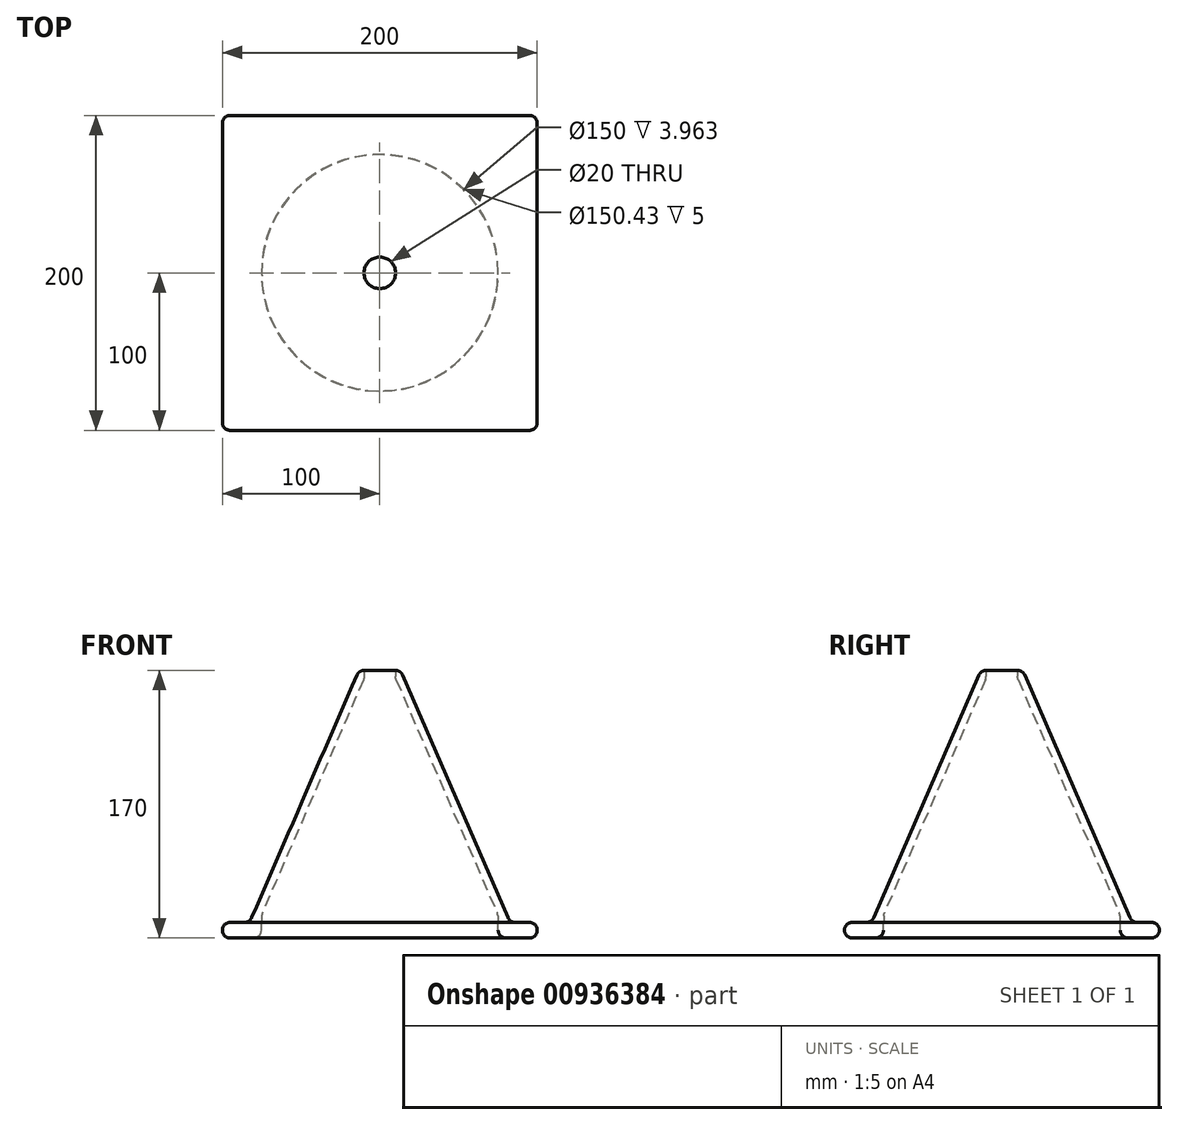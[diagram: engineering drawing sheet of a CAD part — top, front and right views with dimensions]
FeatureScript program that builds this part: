
annotation { "Feature Type Name" : "Feature", "Feature Type Description" : "" }
export const myFeature = defineFeature(function(context is Context, id is Id, definition is map)
    precondition{}
    {
        {
            var Q0;
            Q0=qCreatedBy(makeId("Front.planeOp"),FACE);
            var sketch = newSketch(context, id + "F0", { "sketchPlane" : qUnion([Q0])});
            skPoint(sketch, "E0.middle", {"position": v(0, 0) * mm});
            skLineSegment(sketch, "E1", {"start": v(-10, 75) * mm, "end": v(-75, -75) * mm});
            skLineSegment(sketch, "E2.0", {"start": v(-82.62, -80) * mm, "end": v(-75, -80) * mm});
            skLineSegment(sketch, "E2.1", {"start": v(-13.28, 80) * mm, "end": v(-82.62, -80) * mm});
            skLineSegment(sketch, "E3", {"start": v(-10, 75) * mm, "end": v(-10, 80) * mm});
            skLineSegment(sketch, "E4", {"start": v(-13.28, 80) * mm, "end": v(-10, 80) * mm});
            skLineSegment(sketch, "E5", {"start": v(-75, -75) * mm, "end": v(-75, -80) * mm});
            skLineSegment(sketch, "E6", {"start": v(0, -85.18) * mm, "end": v(0, 91.02) * mm});
            skSolve(sketch);
        }
        {
            var Q0;
            Q0=makeQuery(id+"F0.imprint","IMPRINT",FACE,{"disambiguationData":[TD([[makeQuery(id+"F0.imprint","IMPRINT",EDGE,{"derivedFrom":sQuery(id+"F0.wireOp",EDGE,"E1")}),-1.0]])]});
            var Q1;
            Q1=sQuery(id+"F0.wireOp",EDGE,"E6");
            revolve(context, id + "F1", {"surfaceOperationType" : NewSurfaceOperationType.NEW, "entities" : qUnion([Q0]), "axis" : qUnion([Q1]), "revolveType" : RevolveType.FULL});
        }
        {
            var Q0;
            Q0=makeQuery(id+"F1.opRevolve","SWEPT_FACE",FACE,{"disambiguationData":[OSD([sQuery(id+"F0.wireOp",EDGE,"E2.0")])]});
            var sketch = newSketch(context, id + "F2", { "sketchPlane" : qUnion([Q0])});
            skLineSegment(sketch, "E7.bottom", {"start": v(100, -100) * mm, "end": v(-100, -100) * mm});
            skLineSegment(sketch, "E7.top", {"start": v(100, 100) * mm, "end": v(-100, 100) * mm});
            skLineSegment(sketch, "E7.left", {"start": v(100, -100) * mm, "end": v(100, 100) * mm});
            skLineSegment(sketch, "E7.right", {"start": v(-100, -100) * mm, "end": v(-100, 100) * mm});
            skPoint(sketch, "E7.middle", {"position": v(0, 0) * mm});
            skCircle(sketch, "E8", {"center": v(0, 0) * mm, "radius": 75.22 * mm});
            skSolve(sketch);
        }
        {
            var Q0;
            Q0=makeQuery(id+"F2.imprint","IMPRINT",FACE,{"disambiguationData":[TD([[makeQuery(id+"F2.imprint","IMPRINT",EDGE,{"derivedFrom":sQuery(id+"F2.wireOp",EDGE,"E7.bottom")}),-1.0]])]});
            var Q1;
            Q1=makeQuery(id+"F2.imprint","IMPRINT",FACE,{"disambiguationData":[TD([[makeQuery(id+"F2.imprint","IMPRINT",EDGE,{"derivedFrom":sQuery(id+"F2.wireOp",EDGE,"E8")}),-1.0]])]});
            extrude(context, id + "F3", {"entities" : qUnion([Q0, Q1]), "operationType" : NewBodyOperationType.ADD, "depth" : 10 * mm, "offsetDistance" : 25 * mm});
        }
        {
            var Q0;
            Q0=makeQuery(id+"F3.opExtrude","SWEPT_EDGE",EDGE,{"disambiguationData":[OSD([sQuery(id+"F2.wireOp",EDGE,"E7.bottom"),sQuery(id+"F2.wireOp",EDGE,"E7.right")])]});
            var Q1;
            Q1=makeQuery(id+"F3.opExtrude","SWEPT_EDGE",EDGE,{"disambiguationData":[OSD([sQuery(id+"F2.wireOp",EDGE,"E7.bottom"),sQuery(id+"F2.wireOp",EDGE,"E7.left")])]});
            var Q2;
            Q2=makeQuery(id+"F3.opExtrude","SWEPT_EDGE",EDGE,{"disambiguationData":[OSD([sQuery(id+"F2.wireOp",EDGE,"E7.top"),sQuery(id+"F2.wireOp",EDGE,"E7.left")])]});
            var Q3;
            Q3=makeQuery(id+"F3.opExtrude","CAP_EDGE",EDGE,{"disambiguationData":[OSD([sQuery(id+"F2.wireOp",EDGE,"E8")])],"isStart":false});
            var Q4;
            Q4=makeQuery(id+"F1.opRevolve","SWEPT_EDGE",EDGE,{"disambiguationData":[OSD([sQuery(id+"F0.wireOp",EDGE,"E1"),sQuery(id+"F0.wireOp",EDGE,"E5")])]});
            var Q5;
            Q5=makeQuery(id+"F3.opExtrude","SWEPT_EDGE",EDGE,{"disambiguationData":[OSD([sQuery(id+"F2.wireOp",EDGE,"E7.top"),sQuery(id+"F2.wireOp",EDGE,"E7.right")])]});
            var Q6;
            Q6=makeQuery(id+"F3.opExtrude","CAP_FACE",FACE,{"disambiguationData":[OSD([sQuery(id+"F2.wireOp",EDGE,"E7.bottom"),sQuery(id+"F2.wireOp",EDGE,"E7.top"),sQuery(id+"F2.wireOp",EDGE,"E7.left"),sQuery(id+"F2.wireOp",EDGE,"E7.right"),sQuery(id+"F2.wireOp",EDGE,"E8")])],"isStart":false});
            var Q7;
            Q7=makeQuery(id+"F3.opExtrude","CAP_FACE",FACE,{"disambiguationData":[OSD([sQuery(id+"F2.wireOp",EDGE,"E7.bottom"),sQuery(id+"F2.wireOp",EDGE,"E7.top"),sQuery(id+"F2.wireOp",EDGE,"E7.left"),sQuery(id+"F2.wireOp",EDGE,"E7.right"),sQuery(id+"F2.wireOp",EDGE,"E8")])],"isStart":true});
            var Q8;
            Q8=makeQuery(id+"F1.opRevolve","SWEPT_EDGE",EDGE,{"disambiguationData":[OSD([sQuery(id+"F0.wireOp",EDGE,"E2.1"),sQuery(id+"F0.wireOp",EDGE,"E4")])]});
            var Q9;
            Q9=makeQuery(id+"F1.opRevolve","SWEPT_EDGE",EDGE,{"disambiguationData":[OSD([sQuery(id+"F0.wireOp",EDGE,"E1"),sQuery(id+"F0.wireOp",EDGE,"E3")])]});
            fillet(context, id + "F4", {"entities" : qUnion([Q0, Q1, Q2, Q3, Q4, Q5, Q6, Q7, Q8, Q9]), "radius" : 5 * mm, "tangentPropagation" : true, "allowEdgeOverflow" : false});
        }
    });
